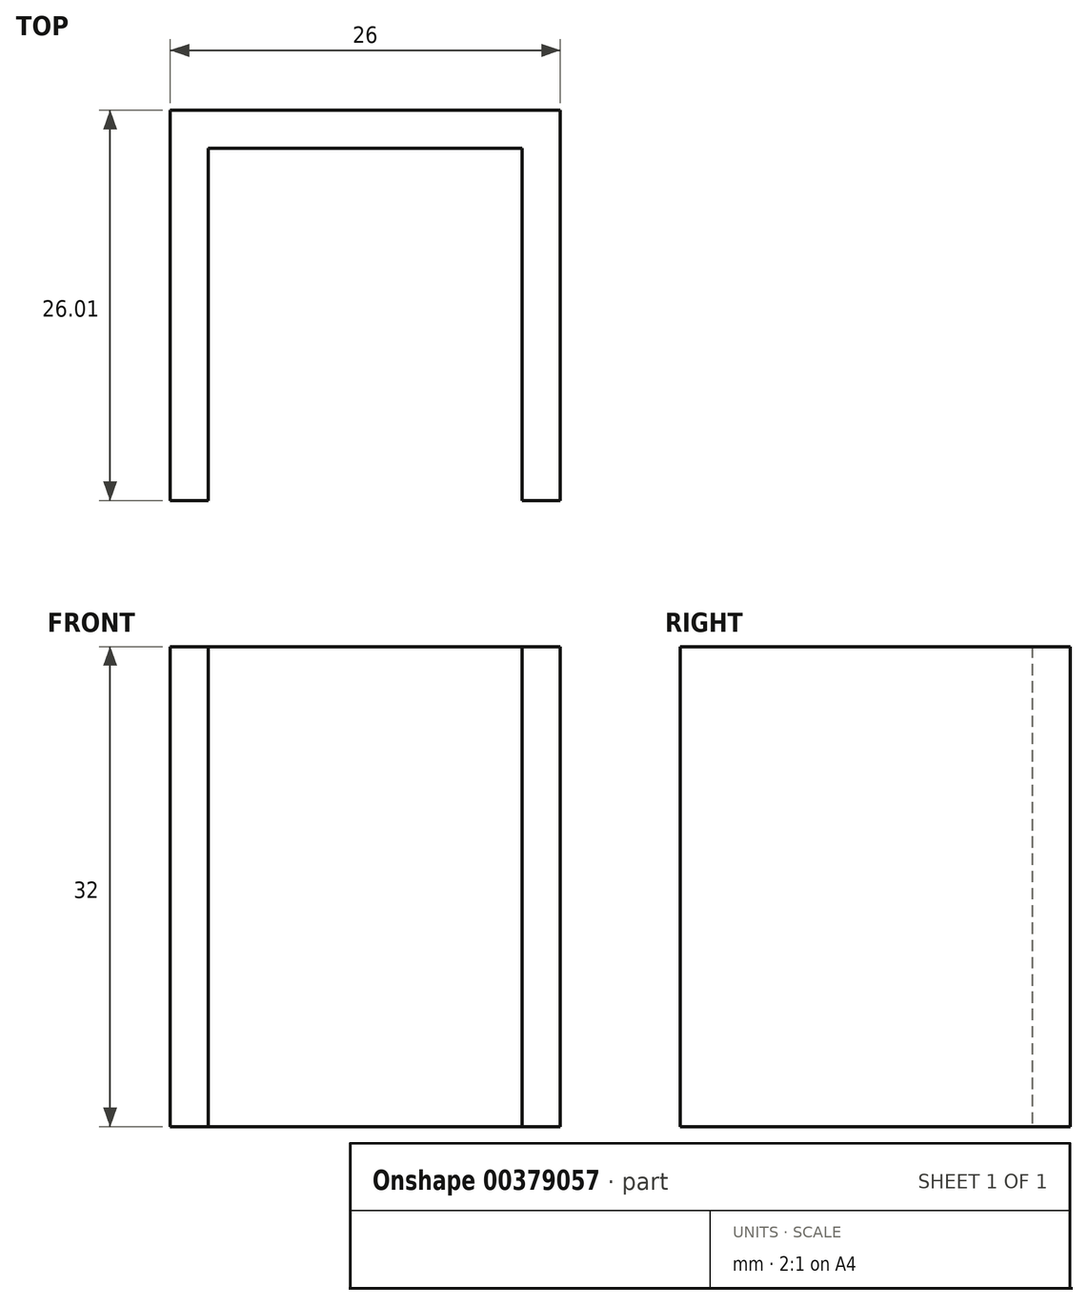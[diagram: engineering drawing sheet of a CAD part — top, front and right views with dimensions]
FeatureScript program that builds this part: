
annotation { "Feature Type Name" : "Feature", "Feature Type Description" : "" }
export const myFeature = defineFeature(function(context is Context, id is Id, definition is map)
    precondition{}
    {
        {
            var Q0;
            Q0=qCreatedBy(makeId("Front.planeOp"),FACE);
            var sketch = newSketch(context, id + "F0", { "sketchPlane" : qUnion([Q0])});
            skLineSegment(sketch, "E0.bottom", {"start": v(-71.3, -25.5) * mm, "end": v(-45.3, -25.5) * mm});
            skLineSegment(sketch, "E0.top", {"start": v(-71.3, -57.5) * mm, "end": v(-45.3, -57.5) * mm});
            skLineSegment(sketch, "E0.left", {"start": v(-71.3, -25.5) * mm, "end": v(-71.3, -57.5) * mm});
            skLineSegment(sketch, "E0.right", {"start": v(-45.3, -25.5) * mm, "end": v(-45.3, -57.5) * mm});
            skSolve(sketch);
        }
        {
            var Q0;
            Q0=makeQuery(id+"F0.imprint","IMPRINT",FACE,{"disambiguationData":[TD([[makeQuery(id+"F0.imprint","IMPRINT",EDGE,{"derivedFrom":sQuery(id+"F0.wireOp",EDGE,"E0.bottom")}),-1.0]])]});
            extrude(context, id + "F1", {"entities" : qUnion([Q0]), "depth" : 26 * mm});
        }
        {
            var Q0;
            Q0=makeQuery(id+"F1.opExtrude","SWEPT_FACE",FACE,{"disambiguationData":[OSD([sQuery(id+"F0.wireOp",EDGE,"E0.top")])]});
            var Q1;
            Q1=makeQuery(id+"F1.opExtrude","CAP_FACE",FACE,{"disambiguationData":[OSD([sQuery(id+"F0.wireOp",EDGE,"E0.bottom"),sQuery(id+"F0.wireOp",EDGE,"E0.top"),sQuery(id+"F0.wireOp",EDGE,"E0.left"),sQuery(id+"F0.wireOp",EDGE,"E0.right")])],"isStart":false});
            var Q2;
            Q2=makeQuery(id+"F1.opExtrude","SWEPT_FACE",FACE,{"disambiguationData":[OSD([sQuery(id+"F0.wireOp",EDGE,"E0.bottom")])]});
            shell(context, id + "F2", {"entities" : qUnion([Q0, Q1, Q2]), "thickness" : 2.54 * mm});
        }
    });
